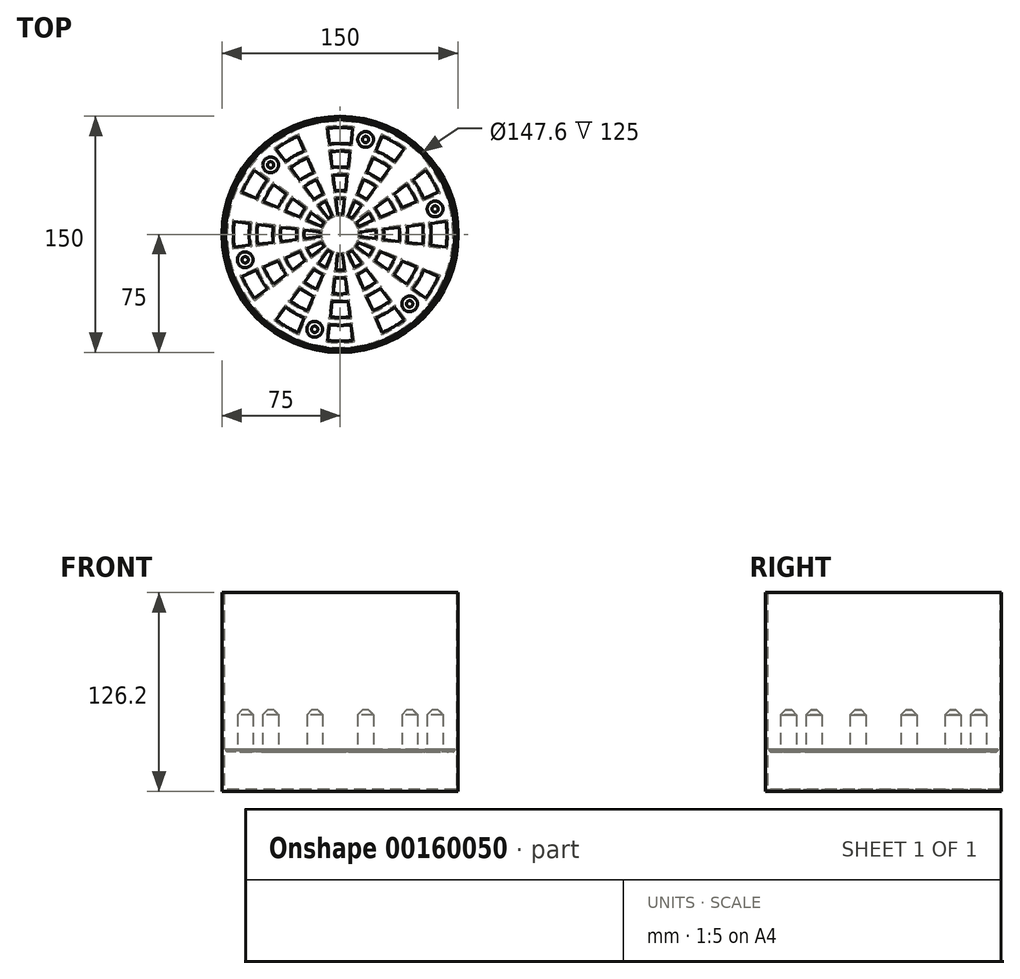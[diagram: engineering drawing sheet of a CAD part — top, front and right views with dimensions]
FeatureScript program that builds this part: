
annotation { "Feature Type Name" : "Feature", "Feature Type Description" : "" }
export const myFeature = defineFeature(function(context is Context, id is Id, definition is map)
    precondition{}
    {
        {
            var Q0;
            Q0=qCreatedBy(makeId("Top.planeOp"),FACE);
            var sketch = newSketch(context, id + "F0", { "sketchPlane" : qUnion([Q0])});
            skCircle(sketch, "E0", {"center": v(0, 0) * mm, "radius": 75 * mm});
            skSolve(sketch);
        }
        {
            var Q0;
            Q0 = qSketchRegion(id + "F0", true);
            extrude(context, id + "F1", {"entities" : qUnion([Q0]), "depth" : 1.2 * mm, "offsetDistance" : 25 * mm});
        }
        {
            var Q0;
            Q0=makeQuery(id+"F1.opExtrude","CAP_FACE",FACE,{"disambiguationData":[OSD([sQuery(id+"F0.wireOp",EDGE,"E0")])],"isStart":false});
            var sketch = newSketch(context, id + "F2", { "sketchPlane" : qUnion([Q0])});
            skCircle(sketch, "E1", {"center": v(0, 0) * mm, "radius": 75 * mm});
            skCircle(sketch, "E2", {"center": v(0, 0) * mm, "radius": 73.8 * mm});
            skSolve(sketch);
        }
        {
            var Q0;
            Q0 = qSketchRegion(id + "F2", true);
            extrude(context, id + "F3", {"entities" : qUnion([Q0]), "operationType" : NewBodyOperationType.ADD, "depth" : 125 * mm, "offsetDistance" : 25 * mm});
        }
        {
            var Q0;
            Q0=qCreatedBy(makeId("Top.planeOp"),FACE);
            cPlane(context, id + "F4", {"entities" : qUnion([Q0]), "cplaneType" : CPlaneType.OFFSET, "offset" : 25 * mm, "width" : 150 * mm, "height" : 150 * mm});
        }
        {
            var Q0;
            Q0=qCreatedBy(id+"F4.planeOp",FACE);
            var sketch = newSketch(context, id + "F5", { "sketchPlane" : qUnion([Q0])});
            skCircle(sketch, "E3", {"center": v(0, 0) * mm, "radius": 72.8 * mm});
            skLineSegment(sketch, "E4", {"start": v(1.51, 12.71) * mm, "end": v(2.7, 22.64) * mm});
            skArc(sketch, "E5", {"start": v(8, 67.33) * mm, "mid": v(0, 67.8) * mm, "end": v(-8, 67.33) * mm});
            skLineSegment(sketch, "E6.MirrorCS", {"start": v(-1.51, 12.71) * mm, "end": v(-2.7, 22.64) * mm});
            skArc(sketch, "E7", {"start": v(6.82, 57.4) * mm, "mid": v(0, 57.8) * mm, "end": v(-6.82, 57.4) * mm});
            skArc(sketch, "E8", {"start": v(6.23, 52.43) * mm, "mid": v(0, 52.8) * mm, "end": v(-6.23, 52.43) * mm});
            skArc(sketch, "E9", {"start": v(5.05, 42.5) * mm, "mid": v(0, 42.8) * mm, "end": v(-5.05, 42.5) * mm});
            skArc(sketch, "E10", {"start": v(4.46, 37.54) * mm, "mid": v(0, 37.8) * mm, "end": v(-4.46, 37.54) * mm});
            skArc(sketch, "E11", {"start": v(3.28, 27.6) * mm, "mid": v(0, 27.8) * mm, "end": v(-3.28, 27.6) * mm});
            skArc(sketch, "E12", {"start": v(2.7, 22.64) * mm, "mid": v(0, 22.8) * mm, "end": v(-2.7, 22.64) * mm});
            skArc(sketch, "E13", {"start": v(1.51, 12.71) * mm, "mid": v(0, 12.8) * mm, "end": v(-1.51, 12.71) * mm});
            skLineSegment(sketch, "E14.trimOffspring", {"start": v(-3.28, 27.6) * mm, "end": v(-4.46, 37.54) * mm});
            skLineSegment(sketch, "E15.trimOffspring", {"start": v(3.28, 27.6) * mm, "end": v(4.46, 37.54) * mm});
            skLineSegment(sketch, "E16.trimOffspring", {"start": v(-5.05, 42.5) * mm, "end": v(-6.23, 52.43) * mm});
            skLineSegment(sketch, "E17.trimOffspring", {"start": v(5.05, 42.5) * mm, "end": v(6.23, 52.43) * mm});
            skLineSegment(sketch, "E18.trimOffspring", {"start": v(-6.82, 57.4) * mm, "end": v(-8, 67.33) * mm});
            skLineSegment(sketch, "E19.trimOffspring", {"start": v(6.82, 57.4) * mm, "end": v(8, 67.33) * mm});
            skArc(sketch, "E20.1.0", {"start": v(-22.8, 53.12) * mm, "mid": v(-28.9, 50.06) * mm, "end": v(-34.6, 46.3) * mm});
            skArc(sketch, "E20.1.1", {"start": v(-16.88, 39.33) * mm, "mid": v(-21.4, 37.07) * mm, "end": v(-25.62, 34.28) * mm});
            skArc(sketch, "E20.1.2", {"start": v(-14.9, 34.74) * mm, "mid": v(-18.9, 32.74) * mm, "end": v(-22.63, 30.28) * mm});
            skArc(sketch, "E20.1.3", {"start": v(-9, 20.95) * mm, "mid": v(-11.4, 19.75) * mm, "end": v(-13.65, 18.26) * mm});
            skLineSegment(sketch, "E20.1.4", {"start": v(-22.8, 53.12) * mm, "end": v(-26.73, 62.3) * mm});
            skLineSegment(sketch, "E20.1.5", {"start": v(-10.96, 25.55) * mm, "end": v(-14.9, 34.74) * mm});
            skArc(sketch, "E20.1.6", {"start": v(-26.73, 62.3) * mm, "mid": v(-33.9, 58.72) * mm, "end": v(-40.6, 54.3) * mm});
            skLineSegment(sketch, "E20.1.7", {"start": v(-16.64, 22.27) * mm, "end": v(-22.63, 30.28) * mm});
            skLineSegment(sketch, "E20.1.8", {"start": v(-25.62, 34.28) * mm, "end": v(-31.61, 42.3) * mm});
            skArc(sketch, "E20.1.9", {"start": v(-20.82, 48.52) * mm, "mid": v(-26.4, 45.73) * mm, "end": v(-31.61, 42.3) * mm});
            skLineSegment(sketch, "E20.1.10", {"start": v(-7.66, 10.25) * mm, "end": v(-13.65, 18.26) * mm});
            skLineSegment(sketch, "E20.1.11", {"start": v(-34.6, 46.3) * mm, "end": v(-40.6, 54.3) * mm});
            skArc(sketch, "E20.1.12", {"start": v(-10.96, 25.55) * mm, "mid": v(-13.9, 24.08) * mm, "end": v(-16.64, 22.27) * mm});
            skLineSegment(sketch, "E20.1.13", {"start": v(-16.88, 39.33) * mm, "end": v(-20.82, 48.52) * mm});
            skLineSegment(sketch, "E20.1.14", {"start": v(-5.05, 11.76) * mm, "end": v(-9, 20.95) * mm});
            skArc(sketch, "E20.1.15", {"start": v(-5.05, 11.76) * mm, "mid": v(-6.4, 11.09) * mm, "end": v(-7.66, 10.25) * mm});
            skArc(sketch, "E20.2.0", {"start": v(-46.3, 34.6) * mm, "mid": v(-50.06, 28.9) * mm, "end": v(-53.12, 22.8) * mm});
            skArc(sketch, "E20.2.1", {"start": v(-34.28, 25.62) * mm, "mid": v(-37.07, 21.4) * mm, "end": v(-39.33, 16.88) * mm});
            skArc(sketch, "E20.2.2", {"start": v(-30.28, 22.63) * mm, "mid": v(-32.74, 18.9) * mm, "end": v(-34.74, 14.9) * mm});
            skArc(sketch, "E20.2.3", {"start": v(-18.26, 13.65) * mm, "mid": v(-19.75, 11.4) * mm, "end": v(-20.95, 9) * mm});
            skLineSegment(sketch, "E20.2.4", {"start": v(-46.3, 34.6) * mm, "end": v(-54.3, 40.6) * mm});
            skLineSegment(sketch, "E20.2.5", {"start": v(-22.27, 16.64) * mm, "end": v(-30.28, 22.63) * mm});
            skArc(sketch, "E20.2.6", {"start": v(-54.3, 40.6) * mm, "mid": v(-58.72, 33.9) * mm, "end": v(-62.3, 26.73) * mm});
            skLineSegment(sketch, "E20.2.7", {"start": v(-25.55, 10.96) * mm, "end": v(-34.74, 14.9) * mm});
            skLineSegment(sketch, "E20.2.8", {"start": v(-39.33, 16.88) * mm, "end": v(-48.52, 20.82) * mm});
            skArc(sketch, "E20.2.9", {"start": v(-42.3, 31.61) * mm, "mid": v(-45.73, 26.4) * mm, "end": v(-48.52, 20.82) * mm});
            skLineSegment(sketch, "E20.2.10", {"start": v(-11.76, 5.05) * mm, "end": v(-20.95, 9) * mm});
            skLineSegment(sketch, "E20.2.11", {"start": v(-53.12, 22.8) * mm, "end": v(-62.3, 26.73) * mm});
            skArc(sketch, "E20.2.12", {"start": v(-22.27, 16.64) * mm, "mid": v(-24.08, 13.9) * mm, "end": v(-25.55, 10.96) * mm});
            skLineSegment(sketch, "E20.2.13", {"start": v(-34.28, 25.62) * mm, "end": v(-42.3, 31.61) * mm});
            skLineSegment(sketch, "E20.2.14", {"start": v(-10.25, 7.66) * mm, "end": v(-18.26, 13.65) * mm});
            skArc(sketch, "E20.2.15", {"start": v(-10.25, 7.66) * mm, "mid": v(-11.09, 6.4) * mm, "end": v(-11.76, 5.05) * mm});
            skArc(sketch, "E20.3.0", {"start": v(-57.4, 6.82) * mm, "mid": v(-57.8, 0) * mm, "end": v(-57.4, -6.82) * mm});
            skArc(sketch, "E20.3.1", {"start": v(-42.5, 5.05) * mm, "mid": v(-42.8, 0) * mm, "end": v(-42.5, -5.05) * mm});
            skArc(sketch, "E20.3.2", {"start": v(-37.54, 4.46) * mm, "mid": v(-37.8, 0) * mm, "end": v(-37.54, -4.46) * mm});
            skArc(sketch, "E20.3.3", {"start": v(-22.64, 2.7) * mm, "mid": v(-22.8, 0) * mm, "end": v(-22.64, -2.7) * mm});
            skLineSegment(sketch, "E20.3.4", {"start": v(-57.4, 6.82) * mm, "end": v(-67.33, 8) * mm});
            skLineSegment(sketch, "E20.3.5", {"start": v(-27.6, 3.28) * mm, "end": v(-37.54, 4.46) * mm});
            skArc(sketch, "E20.3.6", {"start": v(-67.33, 8) * mm, "mid": v(-67.8, 0) * mm, "end": v(-67.33, -8) * mm});
            skLineSegment(sketch, "E20.3.7", {"start": v(-27.6, -3.28) * mm, "end": v(-37.54, -4.46) * mm});
            skLineSegment(sketch, "E20.3.8", {"start": v(-42.5, -5.05) * mm, "end": v(-52.43, -6.23) * mm});
            skArc(sketch, "E20.3.9", {"start": v(-52.43, 6.23) * mm, "mid": v(-52.8, 0) * mm, "end": v(-52.43, -6.23) * mm});
            skLineSegment(sketch, "E20.3.10", {"start": v(-12.71, -1.51) * mm, "end": v(-22.64, -2.7) * mm});
            skLineSegment(sketch, "E20.3.11", {"start": v(-57.4, -6.82) * mm, "end": v(-67.33, -8) * mm});
            skArc(sketch, "E20.3.12", {"start": v(-27.6, 3.28) * mm, "mid": v(-27.8, 0) * mm, "end": v(-27.6, -3.28) * mm});
            skLineSegment(sketch, "E20.3.13", {"start": v(-42.5, 5.05) * mm, "end": v(-52.43, 6.23) * mm});
            skLineSegment(sketch, "E20.3.14", {"start": v(-12.71, 1.51) * mm, "end": v(-22.64, 2.7) * mm});
            skArc(sketch, "E20.3.15", {"start": v(-12.71, 1.51) * mm, "mid": v(-12.8, 0) * mm, "end": v(-12.71, -1.51) * mm});
            skArc(sketch, "E20.4.0", {"start": v(-53.12, -22.8) * mm, "mid": v(-50.06, -28.9) * mm, "end": v(-46.3, -34.6) * mm});
            skArc(sketch, "E20.4.1", {"start": v(-39.33, -16.88) * mm, "mid": v(-37.07, -21.4) * mm, "end": v(-34.28, -25.62) * mm});
            skArc(sketch, "E20.4.2", {"start": v(-34.74, -14.9) * mm, "mid": v(-32.74, -18.9) * mm, "end": v(-30.28, -22.63) * mm});
            skArc(sketch, "E20.4.3", {"start": v(-20.95, -9) * mm, "mid": v(-19.75, -11.4) * mm, "end": v(-18.26, -13.65) * mm});
            skLineSegment(sketch, "E20.4.4", {"start": v(-53.12, -22.8) * mm, "end": v(-62.3, -26.73) * mm});
            skLineSegment(sketch, "E20.4.5", {"start": v(-25.55, -10.96) * mm, "end": v(-34.74, -14.9) * mm});
            skArc(sketch, "E20.4.6", {"start": v(-62.3, -26.73) * mm, "mid": v(-58.72, -33.9) * mm, "end": v(-54.3, -40.6) * mm});
            skLineSegment(sketch, "E20.4.7", {"start": v(-22.27, -16.64) * mm, "end": v(-30.28, -22.63) * mm});
            skLineSegment(sketch, "E20.4.8", {"start": v(-34.28, -25.62) * mm, "end": v(-42.3, -31.61) * mm});
            skArc(sketch, "E20.4.9", {"start": v(-48.52, -20.82) * mm, "mid": v(-45.73, -26.4) * mm, "end": v(-42.3, -31.61) * mm});
            skLineSegment(sketch, "E20.4.10", {"start": v(-10.25, -7.66) * mm, "end": v(-18.26, -13.65) * mm});
            skLineSegment(sketch, "E20.4.11", {"start": v(-46.3, -34.6) * mm, "end": v(-54.3, -40.6) * mm});
            skArc(sketch, "E20.4.12", {"start": v(-25.55, -10.96) * mm, "mid": v(-24.08, -13.9) * mm, "end": v(-22.27, -16.64) * mm});
            skLineSegment(sketch, "E20.4.13", {"start": v(-39.33, -16.88) * mm, "end": v(-48.52, -20.82) * mm});
            skLineSegment(sketch, "E20.4.14", {"start": v(-11.76, -5.05) * mm, "end": v(-20.95, -9) * mm});
            skArc(sketch, "E20.4.15", {"start": v(-11.76, -5.05) * mm, "mid": v(-11.09, -6.4) * mm, "end": v(-10.25, -7.66) * mm});
            skArc(sketch, "E20.5.0", {"start": v(-34.6, -46.3) * mm, "mid": v(-28.9, -50.06) * mm, "end": v(-22.8, -53.12) * mm});
            skArc(sketch, "E20.5.1", {"start": v(-25.62, -34.28) * mm, "mid": v(-21.4, -37.07) * mm, "end": v(-16.88, -39.33) * mm});
            skArc(sketch, "E20.5.2", {"start": v(-22.63, -30.28) * mm, "mid": v(-18.9, -32.74) * mm, "end": v(-14.9, -34.74) * mm});
            skArc(sketch, "E20.5.3", {"start": v(-13.65, -18.26) * mm, "mid": v(-11.4, -19.75) * mm, "end": v(-9, -20.95) * mm});
            skLineSegment(sketch, "E20.5.4", {"start": v(-34.6, -46.3) * mm, "end": v(-40.6, -54.3) * mm});
            skLineSegment(sketch, "E20.5.5", {"start": v(-16.64, -22.27) * mm, "end": v(-22.63, -30.28) * mm});
            skArc(sketch, "E20.5.6", {"start": v(-40.6, -54.3) * mm, "mid": v(-33.9, -58.72) * mm, "end": v(-26.73, -62.3) * mm});
            skLineSegment(sketch, "E20.5.7", {"start": v(-10.96, -25.55) * mm, "end": v(-14.9, -34.74) * mm});
            skLineSegment(sketch, "E20.5.8", {"start": v(-16.88, -39.33) * mm, "end": v(-20.82, -48.52) * mm});
            skArc(sketch, "E20.5.9", {"start": v(-31.61, -42.3) * mm, "mid": v(-26.4, -45.73) * mm, "end": v(-20.82, -48.52) * mm});
            skLineSegment(sketch, "E20.5.10", {"start": v(-5.05, -11.76) * mm, "end": v(-9, -20.95) * mm});
            skLineSegment(sketch, "E20.5.11", {"start": v(-22.8, -53.12) * mm, "end": v(-26.73, -62.3) * mm});
            skArc(sketch, "E20.5.12", {"start": v(-16.64, -22.27) * mm, "mid": v(-13.9, -24.08) * mm, "end": v(-10.96, -25.55) * mm});
            skLineSegment(sketch, "E20.5.13", {"start": v(-25.62, -34.28) * mm, "end": v(-31.61, -42.3) * mm});
            skLineSegment(sketch, "E20.5.14", {"start": v(-7.66, -10.25) * mm, "end": v(-13.65, -18.26) * mm});
            skArc(sketch, "E20.5.15", {"start": v(-7.66, -10.25) * mm, "mid": v(-6.4, -11.09) * mm, "end": v(-5.05, -11.76) * mm});
            skArc(sketch, "E20.6.0", {"start": v(-6.82, -57.4) * mm, "mid": v(0, -57.8) * mm, "end": v(6.82, -57.4) * mm});
            skArc(sketch, "E20.6.1", {"start": v(-5.05, -42.5) * mm, "mid": v(0, -42.8) * mm, "end": v(5.05, -42.5) * mm});
            skArc(sketch, "E20.6.2", {"start": v(-4.46, -37.54) * mm, "mid": v(0, -37.8) * mm, "end": v(4.46, -37.54) * mm});
            skArc(sketch, "E20.6.3", {"start": v(-2.7, -22.64) * mm, "mid": v(0, -22.8) * mm, "end": v(2.7, -22.64) * mm});
            skLineSegment(sketch, "E20.6.4", {"start": v(-6.82, -57.4) * mm, "end": v(-8, -67.33) * mm});
            skLineSegment(sketch, "E20.6.5", {"start": v(-3.28, -27.6) * mm, "end": v(-4.46, -37.54) * mm});
            skArc(sketch, "E20.6.6", {"start": v(-8, -67.33) * mm, "mid": v(0, -67.8) * mm, "end": v(8, -67.33) * mm});
            skLineSegment(sketch, "E20.6.7", {"start": v(3.28, -27.6) * mm, "end": v(4.46, -37.54) * mm});
            skLineSegment(sketch, "E20.6.8", {"start": v(5.05, -42.5) * mm, "end": v(6.23, -52.43) * mm});
            skArc(sketch, "E20.6.9", {"start": v(-6.23, -52.43) * mm, "mid": v(0, -52.8) * mm, "end": v(6.23, -52.43) * mm});
            skLineSegment(sketch, "E20.6.10", {"start": v(1.51, -12.71) * mm, "end": v(2.7, -22.64) * mm});
            skLineSegment(sketch, "E20.6.11", {"start": v(6.82, -57.4) * mm, "end": v(8, -67.33) * mm});
            skArc(sketch, "E20.6.12", {"start": v(-3.28, -27.6) * mm, "mid": v(0, -27.8) * mm, "end": v(3.28, -27.6) * mm});
            skLineSegment(sketch, "E20.6.13", {"start": v(-5.05, -42.5) * mm, "end": v(-6.23, -52.43) * mm});
            skLineSegment(sketch, "E20.6.14", {"start": v(-1.51, -12.71) * mm, "end": v(-2.7, -22.64) * mm});
            skArc(sketch, "E20.6.15", {"start": v(-1.51, -12.71) * mm, "mid": v(0, -12.8) * mm, "end": v(1.51, -12.71) * mm});
            skArc(sketch, "E20.7.0", {"start": v(22.8, -53.12) * mm, "mid": v(28.9, -50.06) * mm, "end": v(34.6, -46.3) * mm});
            skArc(sketch, "E20.7.1", {"start": v(16.88, -39.33) * mm, "mid": v(21.4, -37.07) * mm, "end": v(25.62, -34.28) * mm});
            skArc(sketch, "E20.7.2", {"start": v(14.9, -34.74) * mm, "mid": v(18.9, -32.74) * mm, "end": v(22.63, -30.28) * mm});
            skArc(sketch, "E20.7.3", {"start": v(9, -20.95) * mm, "mid": v(11.4, -19.75) * mm, "end": v(13.65, -18.26) * mm});
            skLineSegment(sketch, "E20.7.4", {"start": v(22.8, -53.12) * mm, "end": v(26.73, -62.3) * mm});
            skLineSegment(sketch, "E20.7.5", {"start": v(10.96, -25.55) * mm, "end": v(14.9, -34.74) * mm});
            skArc(sketch, "E20.7.6", {"start": v(26.73, -62.3) * mm, "mid": v(33.9, -58.72) * mm, "end": v(40.6, -54.3) * mm});
            skLineSegment(sketch, "E20.7.7", {"start": v(16.64, -22.27) * mm, "end": v(22.63, -30.28) * mm});
            skLineSegment(sketch, "E20.7.8", {"start": v(25.62, -34.28) * mm, "end": v(31.61, -42.3) * mm});
            skArc(sketch, "E20.7.9", {"start": v(20.82, -48.52) * mm, "mid": v(26.4, -45.73) * mm, "end": v(31.61, -42.3) * mm});
            skLineSegment(sketch, "E20.7.10", {"start": v(7.66, -10.25) * mm, "end": v(13.65, -18.26) * mm});
            skLineSegment(sketch, "E20.7.11", {"start": v(34.6, -46.3) * mm, "end": v(40.6, -54.3) * mm});
            skArc(sketch, "E20.7.12", {"start": v(10.96, -25.55) * mm, "mid": v(13.9, -24.08) * mm, "end": v(16.64, -22.27) * mm});
            skLineSegment(sketch, "E20.7.13", {"start": v(16.88, -39.33) * mm, "end": v(20.82, -48.52) * mm});
            skLineSegment(sketch, "E20.7.14", {"start": v(5.05, -11.76) * mm, "end": v(9, -20.95) * mm});
            skArc(sketch, "E20.7.15", {"start": v(5.05, -11.76) * mm, "mid": v(6.4, -11.09) * mm, "end": v(7.66, -10.25) * mm});
            skArc(sketch, "E20.8.0", {"start": v(46.3, -34.6) * mm, "mid": v(50.06, -28.9) * mm, "end": v(53.12, -22.8) * mm});
            skArc(sketch, "E20.8.1", {"start": v(34.28, -25.62) * mm, "mid": v(37.07, -21.4) * mm, "end": v(39.33, -16.88) * mm});
            skArc(sketch, "E20.8.2", {"start": v(30.28, -22.63) * mm, "mid": v(32.74, -18.9) * mm, "end": v(34.74, -14.9) * mm});
            skArc(sketch, "E20.8.3", {"start": v(18.26, -13.65) * mm, "mid": v(19.75, -11.4) * mm, "end": v(20.95, -9) * mm});
            skLineSegment(sketch, "E20.8.4", {"start": v(46.3, -34.6) * mm, "end": v(54.3, -40.6) * mm});
            skLineSegment(sketch, "E20.8.5", {"start": v(22.27, -16.64) * mm, "end": v(30.28, -22.63) * mm});
            skArc(sketch, "E20.8.6", {"start": v(54.3, -40.6) * mm, "mid": v(58.72, -33.9) * mm, "end": v(62.3, -26.73) * mm});
            skLineSegment(sketch, "E20.8.7", {"start": v(25.55, -10.96) * mm, "end": v(34.74, -14.9) * mm});
            skLineSegment(sketch, "E20.8.8", {"start": v(39.33, -16.88) * mm, "end": v(48.52, -20.82) * mm});
            skArc(sketch, "E20.8.9", {"start": v(42.3, -31.61) * mm, "mid": v(45.73, -26.4) * mm, "end": v(48.52, -20.82) * mm});
            skLineSegment(sketch, "E20.8.10", {"start": v(11.76, -5.05) * mm, "end": v(20.95, -9) * mm});
            skLineSegment(sketch, "E20.8.11", {"start": v(53.12, -22.8) * mm, "end": v(62.3, -26.73) * mm});
            skArc(sketch, "E20.8.12", {"start": v(22.27, -16.64) * mm, "mid": v(24.08, -13.9) * mm, "end": v(25.55, -10.96) * mm});
            skLineSegment(sketch, "E20.8.13", {"start": v(34.28, -25.62) * mm, "end": v(42.3, -31.61) * mm});
            skLineSegment(sketch, "E20.8.14", {"start": v(10.25, -7.66) * mm, "end": v(18.26, -13.65) * mm});
            skArc(sketch, "E20.8.15", {"start": v(10.25, -7.66) * mm, "mid": v(11.09, -6.4) * mm, "end": v(11.76, -5.05) * mm});
            skArc(sketch, "E20.9.0", {"start": v(57.4, -6.82) * mm, "mid": v(57.8, 0) * mm, "end": v(57.4, 6.82) * mm});
            skArc(sketch, "E20.9.1", {"start": v(42.5, -5.05) * mm, "mid": v(42.8, 0) * mm, "end": v(42.5, 5.05) * mm});
            skArc(sketch, "E20.9.2", {"start": v(37.54, -4.46) * mm, "mid": v(37.8, 0) * mm, "end": v(37.54, 4.46) * mm});
            skArc(sketch, "E20.9.3", {"start": v(22.64, -2.7) * mm, "mid": v(22.8, 0) * mm, "end": v(22.64, 2.7) * mm});
            skLineSegment(sketch, "E20.9.4", {"start": v(57.4, -6.82) * mm, "end": v(67.33, -8) * mm});
            skLineSegment(sketch, "E20.9.5", {"start": v(27.6, -3.28) * mm, "end": v(37.54, -4.46) * mm});
            skArc(sketch, "E20.9.6", {"start": v(67.33, -8) * mm, "mid": v(67.8, 0) * mm, "end": v(67.33, 8) * mm});
            skLineSegment(sketch, "E20.9.7", {"start": v(27.6, 3.28) * mm, "end": v(37.54, 4.46) * mm});
            skLineSegment(sketch, "E20.9.8", {"start": v(42.5, 5.05) * mm, "end": v(52.43, 6.23) * mm});
            skArc(sketch, "E20.9.9", {"start": v(52.43, -6.23) * mm, "mid": v(52.8, 0) * mm, "end": v(52.43, 6.23) * mm});
            skLineSegment(sketch, "E20.9.10", {"start": v(12.71, 1.51) * mm, "end": v(22.64, 2.7) * mm});
            skLineSegment(sketch, "E20.9.11", {"start": v(57.4, 6.82) * mm, "end": v(67.33, 8) * mm});
            skArc(sketch, "E20.9.12", {"start": v(27.6, -3.28) * mm, "mid": v(27.8, 0) * mm, "end": v(27.6, 3.28) * mm});
            skLineSegment(sketch, "E20.9.13", {"start": v(42.5, -5.05) * mm, "end": v(52.43, -6.23) * mm});
            skLineSegment(sketch, "E20.9.14", {"start": v(12.71, -1.51) * mm, "end": v(22.64, -2.7) * mm});
            skArc(sketch, "E20.9.15", {"start": v(12.71, -1.51) * mm, "mid": v(12.8, 0) * mm, "end": v(12.71, 1.51) * mm});
            skArc(sketch, "E21.4.10.0", {"start": v(39.33, 16.88) * mm, "mid": v(37.07, 21.4) * mm, "end": v(34.28, 25.62) * mm});
            skArc(sketch, "E21.8.10.0", {"start": v(34.74, 14.9) * mm, "mid": v(32.74, 18.9) * mm, "end": v(30.28, 22.63) * mm});
            skArc(sketch, "E21.12.10.0", {"start": v(20.95, 9) * mm, "mid": v(19.75, 11.4) * mm, "end": v(18.26, 13.65) * mm});
            skLineSegment(sketch, "E21.16.10.0", {"start": v(53.12, 22.8) * mm, "end": v(62.3, 26.73) * mm});
            skLineSegment(sketch, "E21.19.10.0", {"start": v(25.55, 10.96) * mm, "end": v(34.74, 14.9) * mm});
            skArc(sketch, "E21.22.10.0", {"start": v(62.3, 26.73) * mm, "mid": v(58.72, 33.9) * mm, "end": v(54.3, 40.6) * mm});
            skLineSegment(sketch, "E21.26.10.0", {"start": v(22.27, 16.64) * mm, "end": v(30.28, 22.63) * mm});
            skLineSegment(sketch, "E21.29.10.0", {"start": v(34.28, 25.62) * mm, "end": v(42.3, 31.61) * mm});
            skArc(sketch, "E21.32.10.0", {"start": v(48.52, 20.82) * mm, "mid": v(45.73, 26.4) * mm, "end": v(42.3, 31.61) * mm});
            skLineSegment(sketch, "E21.36.10.0", {"start": v(10.25, 7.66) * mm, "end": v(18.26, 13.65) * mm});
            skArc(sketch, "E21.37.10.0", {"start": v(53.12, 22.8) * mm, "mid": v(50.06, 28.9) * mm, "end": v(46.3, 34.6) * mm});
            skLineSegment(sketch, "E21.39.10.0", {"start": v(46.3, 34.6) * mm, "end": v(54.3, 40.6) * mm});
            skArc(sketch, "E21.42.10.0", {"start": v(25.55, 10.96) * mm, "mid": v(24.08, 13.9) * mm, "end": v(22.27, 16.64) * mm});
            skLineSegment(sketch, "E21.46.10.0", {"start": v(39.33, 16.88) * mm, "end": v(48.52, 20.82) * mm});
            skLineSegment(sketch, "E21.49.10.0", {"start": v(11.76, 5.05) * mm, "end": v(20.95, 9) * mm});
            skArc(sketch, "E21.52.10.0", {"start": v(11.76, 5.05) * mm, "mid": v(11.09, 6.4) * mm, "end": v(10.25, 7.66) * mm});
            skArc(sketch, "E21.4.11.0", {"start": v(25.62, 34.28) * mm, "mid": v(21.4, 37.07) * mm, "end": v(16.88, 39.33) * mm});
            skArc(sketch, "E21.8.11.0", {"start": v(22.63, 30.28) * mm, "mid": v(18.9, 32.74) * mm, "end": v(14.9, 34.74) * mm});
            skArc(sketch, "E21.12.11.0", {"start": v(13.65, 18.26) * mm, "mid": v(11.4, 19.75) * mm, "end": v(9, 20.95) * mm});
            skLineSegment(sketch, "E21.16.11.0", {"start": v(34.6, 46.3) * mm, "end": v(40.6, 54.3) * mm});
            skLineSegment(sketch, "E21.19.11.0", {"start": v(16.64, 22.27) * mm, "end": v(22.63, 30.28) * mm});
            skArc(sketch, "E21.22.11.0", {"start": v(40.6, 54.3) * mm, "mid": v(33.9, 58.72) * mm, "end": v(26.73, 62.3) * mm});
            skLineSegment(sketch, "E21.26.11.0", {"start": v(10.96, 25.55) * mm, "end": v(14.9, 34.74) * mm});
            skLineSegment(sketch, "E21.29.11.0", {"start": v(16.88, 39.33) * mm, "end": v(20.82, 48.52) * mm});
            skArc(sketch, "E21.32.11.0", {"start": v(31.61, 42.3) * mm, "mid": v(26.4, 45.73) * mm, "end": v(20.82, 48.52) * mm});
            skLineSegment(sketch, "E21.36.11.0", {"start": v(5.05, 11.76) * mm, "end": v(9, 20.95) * mm});
            skArc(sketch, "E21.37.11.0", {"start": v(34.6, 46.3) * mm, "mid": v(28.9, 50.06) * mm, "end": v(22.8, 53.12) * mm});
            skLineSegment(sketch, "E21.39.11.0", {"start": v(22.8, 53.12) * mm, "end": v(26.73, 62.3) * mm});
            skArc(sketch, "E21.42.11.0", {"start": v(16.64, 22.27) * mm, "mid": v(13.9, 24.08) * mm, "end": v(10.96, 25.55) * mm});
            skLineSegment(sketch, "E21.46.11.0", {"start": v(25.62, 34.28) * mm, "end": v(31.61, 42.3) * mm});
            skLineSegment(sketch, "E21.49.11.0", {"start": v(7.66, 10.25) * mm, "end": v(13.65, 18.26) * mm});
            skArc(sketch, "E21.52.11.0", {"start": v(7.66, 10.25) * mm, "mid": v(6.4, 11.09) * mm, "end": v(5.05, 11.76) * mm});
            skSolve(sketch);
        }
        {
            var Q0;
            Q0 = qSketchRegion(id + "F5", true);
            extrude(context, id + "F6", {"entities" : qUnion([Q0]), "depth" : 1.6 * mm, "offsetDistance" : 25 * mm});
        }
        {
            var Q0;
            Q0=makeQuery(id+"F6.opExtrude","CAP_FACE",FACE,{"disambiguationData":[OSD([sQuery(id+"F5.wireOp",EDGE,"E3"),sQuery(id+"F5.wireOp",EDGE,"E4"),sQuery(id+"F5.wireOp",EDGE,"E5"),sQuery(id+"F5.wireOp",EDGE,"E6.MirrorCS"),sQuery(id+"F5.wireOp",EDGE,"E7"),sQuery(id+"F5.wireOp",EDGE,"E8"),sQuery(id+"F5.wireOp",EDGE,"E9"),sQuery(id+"F5.wireOp",EDGE,"E10"),sQuery(id+"F5.wireOp",EDGE,"E11"),sQuery(id+"F5.wireOp",EDGE,"E12"),sQuery(id+"F5.wireOp",EDGE,"E13"),sQuery(id+"F5.wireOp",EDGE,"E14.trimOffspring"),sQuery(id+"F5.wireOp",EDGE,"E15.trimOffspring"),sQuery(id+"F5.wireOp",EDGE,"E16.trimOffspring"),sQuery(id+"F5.wireOp",EDGE,"E17.trimOffspring"),sQuery(id+"F5.wireOp",EDGE,"E18.trimOffspring"),sQuery(id+"F5.wireOp",EDGE,"E19.trimOffspring"),sQuery(id+"F5.wireOp",EDGE,"E20.1.0"),sQuery(id+"F5.wireOp",EDGE,"E20.1.1"),sQuery(id+"F5.wireOp",EDGE,"E20.1.2"),sQuery(id+"F5.wireOp",EDGE,"E20.1.3"),sQuery(id+"F5.wireOp",EDGE,"E20.1.4"),sQuery(id+"F5.wireOp",EDGE,"E20.1.5"),sQuery(id+"F5.wireOp",EDGE,"E20.1.6"),sQuery(id+"F5.wireOp",EDGE,"E20.1.7"),sQuery(id+"F5.wireOp",EDGE,"E20.1.8"),sQuery(id+"F5.wireOp",EDGE,"E20.1.9"),sQuery(id+"F5.wireOp",EDGE,"E20.1.10"),sQuery(id+"F5.wireOp",EDGE,"E20.1.11"),sQuery(id+"F5.wireOp",EDGE,"E20.1.12"),sQuery(id+"F5.wireOp",EDGE,"E20.1.13"),sQuery(id+"F5.wireOp",EDGE,"E20.1.14"),sQuery(id+"F5.wireOp",EDGE,"E20.1.15"),sQuery(id+"F5.wireOp",EDGE,"E20.2.0"),sQuery(id+"F5.wireOp",EDGE,"E20.2.1"),sQuery(id+"F5.wireOp",EDGE,"E20.2.2"),sQuery(id+"F5.wireOp",EDGE,"E20.2.3"),sQuery(id+"F5.wireOp",EDGE,"E20.2.4"),sQuery(id+"F5.wireOp",EDGE,"E20.2.5"),sQuery(id+"F5.wireOp",EDGE,"E20.2.6"),sQuery(id+"F5.wireOp",EDGE,"E20.2.7"),sQuery(id+"F5.wireOp",EDGE,"E20.2.8"),sQuery(id+"F5.wireOp",EDGE,"E20.2.9"),sQuery(id+"F5.wireOp",EDGE,"E20.2.10"),sQuery(id+"F5.wireOp",EDGE,"E20.2.11"),sQuery(id+"F5.wireOp",EDGE,"E20.2.12"),sQuery(id+"F5.wireOp",EDGE,"E20.2.13"),sQuery(id+"F5.wireOp",EDGE,"E20.2.14"),sQuery(id+"F5.wireOp",EDGE,"E20.2.15"),sQuery(id+"F5.wireOp",EDGE,"E20.3.0"),sQuery(id+"F5.wireOp",EDGE,"E20.3.1"),sQuery(id+"F5.wireOp",EDGE,"E20.3.2"),sQuery(id+"F5.wireOp",EDGE,"E20.3.3"),sQuery(id+"F5.wireOp",EDGE,"E20.3.4"),sQuery(id+"F5.wireOp",EDGE,"E20.3.5"),sQuery(id+"F5.wireOp",EDGE,"E20.3.6"),sQuery(id+"F5.wireOp",EDGE,"E20.3.7"),sQuery(id+"F5.wireOp",EDGE,"E20.3.8"),sQuery(id+"F5.wireOp",EDGE,"E20.3.9"),sQuery(id+"F5.wireOp",EDGE,"E20.3.10"),sQuery(id+"F5.wireOp",EDGE,"E20.3.11"),sQuery(id+"F5.wireOp",EDGE,"E20.3.12"),sQuery(id+"F5.wireOp",EDGE,"E20.3.13"),sQuery(id+"F5.wireOp",EDGE,"E20.3.14"),sQuery(id+"F5.wireOp",EDGE,"E20.3.15"),sQuery(id+"F5.wireOp",EDGE,"E20.4.0"),sQuery(id+"F5.wireOp",EDGE,"E20.4.1"),sQuery(id+"F5.wireOp",EDGE,"E20.4.2"),sQuery(id+"F5.wireOp",EDGE,"E20.4.3"),sQuery(id+"F5.wireOp",EDGE,"E20.4.4"),sQuery(id+"F5.wireOp",EDGE,"E20.4.5"),sQuery(id+"F5.wireOp",EDGE,"E20.4.6"),sQuery(id+"F5.wireOp",EDGE,"E20.4.7"),sQuery(id+"F5.wireOp",EDGE,"E20.4.8"),sQuery(id+"F5.wireOp",EDGE,"E20.4.9"),sQuery(id+"F5.wireOp",EDGE,"E20.4.10"),sQuery(id+"F5.wireOp",EDGE,"E20.4.11"),sQuery(id+"F5.wireOp",EDGE,"E20.4.12"),sQuery(id+"F5.wireOp",EDGE,"E20.4.13"),sQuery(id+"F5.wireOp",EDGE,"E20.4.14"),sQuery(id+"F5.wireOp",EDGE,"E20.4.15"),sQuery(id+"F5.wireOp",EDGE,"E20.5.0"),sQuery(id+"F5.wireOp",EDGE,"E20.5.1"),sQuery(id+"F5.wireOp",EDGE,"E20.5.2"),sQuery(id+"F5.wireOp",EDGE,"E20.5.3"),sQuery(id+"F5.wireOp",EDGE,"E20.5.4"),sQuery(id+"F5.wireOp",EDGE,"E20.5.5"),sQuery(id+"F5.wireOp",EDGE,"E20.5.6"),sQuery(id+"F5.wireOp",EDGE,"E20.5.7"),sQuery(id+"F5.wireOp",EDGE,"E20.5.8"),sQuery(id+"F5.wireOp",EDGE,"E20.5.9"),sQuery(id+"F5.wireOp",EDGE,"E20.5.10"),sQuery(id+"F5.wireOp",EDGE,"E20.5.11"),sQuery(id+"F5.wireOp",EDGE,"E20.5.12"),sQuery(id+"F5.wireOp",EDGE,"E20.5.13"),sQuery(id+"F5.wireOp",EDGE,"E20.5.14"),sQuery(id+"F5.wireOp",EDGE,"E20.5.15"),sQuery(id+"F5.wireOp",EDGE,"E20.6.0"),sQuery(id+"F5.wireOp",EDGE,"E20.6.1"),sQuery(id+"F5.wireOp",EDGE,"E20.6.2"),sQuery(id+"F5.wireOp",EDGE,"E20.6.3"),sQuery(id+"F5.wireOp",EDGE,"E20.6.4"),sQuery(id+"F5.wireOp",EDGE,"E20.6.5"),sQuery(id+"F5.wireOp",EDGE,"E20.6.6"),sQuery(id+"F5.wireOp",EDGE,"E20.6.7"),sQuery(id+"F5.wireOp",EDGE,"E20.6.8"),sQuery(id+"F5.wireOp",EDGE,"E20.6.9"),sQuery(id+"F5.wireOp",EDGE,"E20.6.10"),sQuery(id+"F5.wireOp",EDGE,"E20.6.11"),sQuery(id+"F5.wireOp",EDGE,"E20.6.12"),sQuery(id+"F5.wireOp",EDGE,"E20.6.13"),sQuery(id+"F5.wireOp",EDGE,"E20.6.14"),sQuery(id+"F5.wireOp",EDGE,"E20.6.15"),sQuery(id+"F5.wireOp",EDGE,"E20.7.0"),sQuery(id+"F5.wireOp",EDGE,"E20.7.1"),sQuery(id+"F5.wireOp",EDGE,"E20.7.2"),sQuery(id+"F5.wireOp",EDGE,"E20.7.3"),sQuery(id+"F5.wireOp",EDGE,"E20.7.4"),sQuery(id+"F5.wireOp",EDGE,"E20.7.5"),sQuery(id+"F5.wireOp",EDGE,"E20.7.6"),sQuery(id+"F5.wireOp",EDGE,"E20.7.7"),sQuery(id+"F5.wireOp",EDGE,"E20.7.8"),sQuery(id+"F5.wireOp",EDGE,"E20.7.9"),sQuery(id+"F5.wireOp",EDGE,"E20.7.10"),sQuery(id+"F5.wireOp",EDGE,"E20.7.11"),sQuery(id+"F5.wireOp",EDGE,"E20.7.12"),sQuery(id+"F5.wireOp",EDGE,"E20.7.13"),sQuery(id+"F5.wireOp",EDGE,"E20.7.14"),sQuery(id+"F5.wireOp",EDGE,"E20.7.15"),sQuery(id+"F5.wireOp",EDGE,"E20.8.0"),sQuery(id+"F5.wireOp",EDGE,"E20.8.1"),sQuery(id+"F5.wireOp",EDGE,"E20.8.2"),sQuery(id+"F5.wireOp",EDGE,"E20.8.3"),sQuery(id+"F5.wireOp",EDGE,"E20.8.4"),sQuery(id+"F5.wireOp",EDGE,"E20.8.5"),sQuery(id+"F5.wireOp",EDGE,"E20.8.6"),sQuery(id+"F5.wireOp",EDGE,"E20.8.7"),sQuery(id+"F5.wireOp",EDGE,"E20.8.8"),sQuery(id+"F5.wireOp",EDGE,"E20.8.9"),sQuery(id+"F5.wireOp",EDGE,"E20.8.10"),sQuery(id+"F5.wireOp",EDGE,"E20.8.11"),sQuery(id+"F5.wireOp",EDGE,"E20.8.12"),sQuery(id+"F5.wireOp",EDGE,"E20.8.13"),sQuery(id+"F5.wireOp",EDGE,"E20.8.14"),sQuery(id+"F5.wireOp",EDGE,"E20.8.15"),sQuery(id+"F5.wireOp",EDGE,"E20.9.0"),sQuery(id+"F5.wireOp",EDGE,"E20.9.1"),sQuery(id+"F5.wireOp",EDGE,"E20.9.2"),sQuery(id+"F5.wireOp",EDGE,"E20.9.3"),sQuery(id+"F5.wireOp",EDGE,"E20.9.4"),sQuery(id+"F5.wireOp",EDGE,"E20.9.5"),sQuery(id+"F5.wireOp",EDGE,"E20.9.6"),sQuery(id+"F5.wireOp",EDGE,"E20.9.7"),sQuery(id+"F5.wireOp",EDGE,"E20.9.8"),sQuery(id+"F5.wireOp",EDGE,"E20.9.9"),sQuery(id+"F5.wireOp",EDGE,"E20.9.10"),sQuery(id+"F5.wireOp",EDGE,"E20.9.11"),sQuery(id+"F5.wireOp",EDGE,"E20.9.12"),sQuery(id+"F5.wireOp",EDGE,"E20.9.13"),sQuery(id+"F5.wireOp",EDGE,"E20.9.14"),sQuery(id+"F5.wireOp",EDGE,"E20.9.15"),sQuery(id+"F5.wireOp",EDGE,"E21.4.10.0"),sQuery(id+"F5.wireOp",EDGE,"E21.8.10.0"),sQuery(id+"F5.wireOp",EDGE,"E21.12.10.0"),sQuery(id+"F5.wireOp",EDGE,"E21.16.10.0"),sQuery(id+"F5.wireOp",EDGE,"E21.19.10.0"),sQuery(id+"F5.wireOp",EDGE,"E21.22.10.0"),sQuery(id+"F5.wireOp",EDGE,"E21.26.10.0"),sQuery(id+"F5.wireOp",EDGE,"E21.29.10.0"),sQuery(id+"F5.wireOp",EDGE,"E21.32.10.0"),sQuery(id+"F5.wireOp",EDGE,"E21.36.10.0"),sQuery(id+"F5.wireOp",EDGE,"E21.37.10.0"),sQuery(id+"F5.wireOp",EDGE,"E21.39.10.0"),sQuery(id+"F5.wireOp",EDGE,"E21.42.10.0"),sQuery(id+"F5.wireOp",EDGE,"E21.46.10.0"),sQuery(id+"F5.wireOp",EDGE,"E21.49.10.0"),sQuery(id+"F5.wireOp",EDGE,"E21.52.10.0"),sQuery(id+"F5.wireOp",EDGE,"E21.4.11.0"),sQuery(id+"F5.wireOp",EDGE,"E21.8.11.0"),sQuery(id+"F5.wireOp",EDGE,"E21.12.11.0"),sQuery(id+"F5.wireOp",EDGE,"E21.16.11.0"),sQuery(id+"F5.wireOp",EDGE,"E21.19.11.0"),sQuery(id+"F5.wireOp",EDGE,"E21.22.11.0"),sQuery(id+"F5.wireOp",EDGE,"E21.26.11.0"),sQuery(id+"F5.wireOp",EDGE,"E21.29.11.0"),sQuery(id+"F5.wireOp",EDGE,"E21.32.11.0"),sQuery(id+"F5.wireOp",EDGE,"E21.36.11.0"),sQuery(id+"F5.wireOp",EDGE,"E21.37.11.0"),sQuery(id+"F5.wireOp",EDGE,"E21.39.11.0"),sQuery(id+"F5.wireOp",EDGE,"E21.42.11.0"),sQuery(id+"F5.wireOp",EDGE,"E21.46.11.0"),sQuery(id+"F5.wireOp",EDGE,"E21.49.11.0"),sQuery(id+"F5.wireOp",EDGE,"E21.52.11.0")])],"isStart":true});
            chamfer(context, id + "F7", {"entities" : qUnion([Q0]), "width" : 1 * mm, "tangentPropagation" : true});
        }
        {
            var Q0;
            Q0=makeQuery(id+"F6.opExtrude","CAP_FACE",FACE,{"disambiguationData":[OSD([sQuery(id+"F5.wireOp",EDGE,"E3"),sQuery(id+"F5.wireOp",EDGE,"E4"),sQuery(id+"F5.wireOp",EDGE,"E5"),sQuery(id+"F5.wireOp",EDGE,"E6.MirrorCS"),sQuery(id+"F5.wireOp",EDGE,"E7"),sQuery(id+"F5.wireOp",EDGE,"E8"),sQuery(id+"F5.wireOp",EDGE,"E9"),sQuery(id+"F5.wireOp",EDGE,"E10"),sQuery(id+"F5.wireOp",EDGE,"E11"),sQuery(id+"F5.wireOp",EDGE,"E12"),sQuery(id+"F5.wireOp",EDGE,"E13"),sQuery(id+"F5.wireOp",EDGE,"E14.trimOffspring"),sQuery(id+"F5.wireOp",EDGE,"E15.trimOffspring"),sQuery(id+"F5.wireOp",EDGE,"E16.trimOffspring"),sQuery(id+"F5.wireOp",EDGE,"E17.trimOffspring"),sQuery(id+"F5.wireOp",EDGE,"E18.trimOffspring"),sQuery(id+"F5.wireOp",EDGE,"E19.trimOffspring"),sQuery(id+"F5.wireOp",EDGE,"E20.1.0"),sQuery(id+"F5.wireOp",EDGE,"E20.1.1"),sQuery(id+"F5.wireOp",EDGE,"E20.1.2"),sQuery(id+"F5.wireOp",EDGE,"E20.1.3"),sQuery(id+"F5.wireOp",EDGE,"E20.1.4"),sQuery(id+"F5.wireOp",EDGE,"E20.1.5"),sQuery(id+"F5.wireOp",EDGE,"E20.1.6"),sQuery(id+"F5.wireOp",EDGE,"E20.1.7"),sQuery(id+"F5.wireOp",EDGE,"E20.1.8"),sQuery(id+"F5.wireOp",EDGE,"E20.1.9"),sQuery(id+"F5.wireOp",EDGE,"E20.1.10"),sQuery(id+"F5.wireOp",EDGE,"E20.1.11"),sQuery(id+"F5.wireOp",EDGE,"E20.1.12"),sQuery(id+"F5.wireOp",EDGE,"E20.1.13"),sQuery(id+"F5.wireOp",EDGE,"E20.1.14"),sQuery(id+"F5.wireOp",EDGE,"E20.1.15"),sQuery(id+"F5.wireOp",EDGE,"E20.2.0"),sQuery(id+"F5.wireOp",EDGE,"E20.2.1"),sQuery(id+"F5.wireOp",EDGE,"E20.2.2"),sQuery(id+"F5.wireOp",EDGE,"E20.2.3"),sQuery(id+"F5.wireOp",EDGE,"E20.2.4"),sQuery(id+"F5.wireOp",EDGE,"E20.2.5"),sQuery(id+"F5.wireOp",EDGE,"E20.2.6"),sQuery(id+"F5.wireOp",EDGE,"E20.2.7"),sQuery(id+"F5.wireOp",EDGE,"E20.2.8"),sQuery(id+"F5.wireOp",EDGE,"E20.2.9"),sQuery(id+"F5.wireOp",EDGE,"E20.2.10"),sQuery(id+"F5.wireOp",EDGE,"E20.2.11"),sQuery(id+"F5.wireOp",EDGE,"E20.2.12"),sQuery(id+"F5.wireOp",EDGE,"E20.2.13"),sQuery(id+"F5.wireOp",EDGE,"E20.2.14"),sQuery(id+"F5.wireOp",EDGE,"E20.2.15"),sQuery(id+"F5.wireOp",EDGE,"E20.3.0"),sQuery(id+"F5.wireOp",EDGE,"E20.3.1"),sQuery(id+"F5.wireOp",EDGE,"E20.3.2"),sQuery(id+"F5.wireOp",EDGE,"E20.3.3"),sQuery(id+"F5.wireOp",EDGE,"E20.3.4"),sQuery(id+"F5.wireOp",EDGE,"E20.3.5"),sQuery(id+"F5.wireOp",EDGE,"E20.3.6"),sQuery(id+"F5.wireOp",EDGE,"E20.3.7"),sQuery(id+"F5.wireOp",EDGE,"E20.3.8"),sQuery(id+"F5.wireOp",EDGE,"E20.3.9"),sQuery(id+"F5.wireOp",EDGE,"E20.3.10"),sQuery(id+"F5.wireOp",EDGE,"E20.3.11"),sQuery(id+"F5.wireOp",EDGE,"E20.3.12"),sQuery(id+"F5.wireOp",EDGE,"E20.3.13"),sQuery(id+"F5.wireOp",EDGE,"E20.3.14"),sQuery(id+"F5.wireOp",EDGE,"E20.3.15"),sQuery(id+"F5.wireOp",EDGE,"E20.4.0"),sQuery(id+"F5.wireOp",EDGE,"E20.4.1"),sQuery(id+"F5.wireOp",EDGE,"E20.4.2"),sQuery(id+"F5.wireOp",EDGE,"E20.4.3"),sQuery(id+"F5.wireOp",EDGE,"E20.4.4"),sQuery(id+"F5.wireOp",EDGE,"E20.4.5"),sQuery(id+"F5.wireOp",EDGE,"E20.4.6"),sQuery(id+"F5.wireOp",EDGE,"E20.4.7"),sQuery(id+"F5.wireOp",EDGE,"E20.4.8"),sQuery(id+"F5.wireOp",EDGE,"E20.4.9"),sQuery(id+"F5.wireOp",EDGE,"E20.4.10"),sQuery(id+"F5.wireOp",EDGE,"E20.4.11"),sQuery(id+"F5.wireOp",EDGE,"E20.4.12"),sQuery(id+"F5.wireOp",EDGE,"E20.4.13"),sQuery(id+"F5.wireOp",EDGE,"E20.4.14"),sQuery(id+"F5.wireOp",EDGE,"E20.4.15"),sQuery(id+"F5.wireOp",EDGE,"E20.5.0"),sQuery(id+"F5.wireOp",EDGE,"E20.5.1"),sQuery(id+"F5.wireOp",EDGE,"E20.5.2"),sQuery(id+"F5.wireOp",EDGE,"E20.5.3"),sQuery(id+"F5.wireOp",EDGE,"E20.5.4"),sQuery(id+"F5.wireOp",EDGE,"E20.5.5"),sQuery(id+"F5.wireOp",EDGE,"E20.5.6"),sQuery(id+"F5.wireOp",EDGE,"E20.5.7"),sQuery(id+"F5.wireOp",EDGE,"E20.5.8"),sQuery(id+"F5.wireOp",EDGE,"E20.5.9"),sQuery(id+"F5.wireOp",EDGE,"E20.5.10"),sQuery(id+"F5.wireOp",EDGE,"E20.5.11"),sQuery(id+"F5.wireOp",EDGE,"E20.5.12"),sQuery(id+"F5.wireOp",EDGE,"E20.5.13"),sQuery(id+"F5.wireOp",EDGE,"E20.5.14"),sQuery(id+"F5.wireOp",EDGE,"E20.5.15"),sQuery(id+"F5.wireOp",EDGE,"E20.6.0"),sQuery(id+"F5.wireOp",EDGE,"E20.6.1"),sQuery(id+"F5.wireOp",EDGE,"E20.6.2"),sQuery(id+"F5.wireOp",EDGE,"E20.6.3"),sQuery(id+"F5.wireOp",EDGE,"E20.6.4"),sQuery(id+"F5.wireOp",EDGE,"E20.6.5"),sQuery(id+"F5.wireOp",EDGE,"E20.6.6"),sQuery(id+"F5.wireOp",EDGE,"E20.6.7"),sQuery(id+"F5.wireOp",EDGE,"E20.6.8"),sQuery(id+"F5.wireOp",EDGE,"E20.6.9"),sQuery(id+"F5.wireOp",EDGE,"E20.6.10"),sQuery(id+"F5.wireOp",EDGE,"E20.6.11"),sQuery(id+"F5.wireOp",EDGE,"E20.6.12"),sQuery(id+"F5.wireOp",EDGE,"E20.6.13"),sQuery(id+"F5.wireOp",EDGE,"E20.6.14"),sQuery(id+"F5.wireOp",EDGE,"E20.6.15"),sQuery(id+"F5.wireOp",EDGE,"E20.7.0"),sQuery(id+"F5.wireOp",EDGE,"E20.7.1"),sQuery(id+"F5.wireOp",EDGE,"E20.7.2"),sQuery(id+"F5.wireOp",EDGE,"E20.7.3"),sQuery(id+"F5.wireOp",EDGE,"E20.7.4"),sQuery(id+"F5.wireOp",EDGE,"E20.7.5"),sQuery(id+"F5.wireOp",EDGE,"E20.7.6"),sQuery(id+"F5.wireOp",EDGE,"E20.7.7"),sQuery(id+"F5.wireOp",EDGE,"E20.7.8"),sQuery(id+"F5.wireOp",EDGE,"E20.7.9"),sQuery(id+"F5.wireOp",EDGE,"E20.7.10"),sQuery(id+"F5.wireOp",EDGE,"E20.7.11"),sQuery(id+"F5.wireOp",EDGE,"E20.7.12"),sQuery(id+"F5.wireOp",EDGE,"E20.7.13"),sQuery(id+"F5.wireOp",EDGE,"E20.7.14"),sQuery(id+"F5.wireOp",EDGE,"E20.7.15"),sQuery(id+"F5.wireOp",EDGE,"E20.8.0"),sQuery(id+"F5.wireOp",EDGE,"E20.8.1"),sQuery(id+"F5.wireOp",EDGE,"E20.8.2"),sQuery(id+"F5.wireOp",EDGE,"E20.8.3"),sQuery(id+"F5.wireOp",EDGE,"E20.8.4"),sQuery(id+"F5.wireOp",EDGE,"E20.8.5"),sQuery(id+"F5.wireOp",EDGE,"E20.8.6"),sQuery(id+"F5.wireOp",EDGE,"E20.8.7"),sQuery(id+"F5.wireOp",EDGE,"E20.8.8"),sQuery(id+"F5.wireOp",EDGE,"E20.8.9"),sQuery(id+"F5.wireOp",EDGE,"E20.8.10"),sQuery(id+"F5.wireOp",EDGE,"E20.8.11"),sQuery(id+"F5.wireOp",EDGE,"E20.8.12"),sQuery(id+"F5.wireOp",EDGE,"E20.8.13"),sQuery(id+"F5.wireOp",EDGE,"E20.8.14"),sQuery(id+"F5.wireOp",EDGE,"E20.8.15"),sQuery(id+"F5.wireOp",EDGE,"E20.9.0"),sQuery(id+"F5.wireOp",EDGE,"E20.9.1"),sQuery(id+"F5.wireOp",EDGE,"E20.9.2"),sQuery(id+"F5.wireOp",EDGE,"E20.9.3"),sQuery(id+"F5.wireOp",EDGE,"E20.9.4"),sQuery(id+"F5.wireOp",EDGE,"E20.9.5"),sQuery(id+"F5.wireOp",EDGE,"E20.9.6"),sQuery(id+"F5.wireOp",EDGE,"E20.9.7"),sQuery(id+"F5.wireOp",EDGE,"E20.9.8"),sQuery(id+"F5.wireOp",EDGE,"E20.9.9"),sQuery(id+"F5.wireOp",EDGE,"E20.9.10"),sQuery(id+"F5.wireOp",EDGE,"E20.9.11"),sQuery(id+"F5.wireOp",EDGE,"E20.9.12"),sQuery(id+"F5.wireOp",EDGE,"E20.9.13"),sQuery(id+"F5.wireOp",EDGE,"E20.9.14"),sQuery(id+"F5.wireOp",EDGE,"E20.9.15"),sQuery(id+"F5.wireOp",EDGE,"E21.4.10.0"),sQuery(id+"F5.wireOp",EDGE,"E21.8.10.0"),sQuery(id+"F5.wireOp",EDGE,"E21.12.10.0"),sQuery(id+"F5.wireOp",EDGE,"E21.16.10.0"),sQuery(id+"F5.wireOp",EDGE,"E21.19.10.0"),sQuery(id+"F5.wireOp",EDGE,"E21.22.10.0"),sQuery(id+"F5.wireOp",EDGE,"E21.26.10.0"),sQuery(id+"F5.wireOp",EDGE,"E21.29.10.0"),sQuery(id+"F5.wireOp",EDGE,"E21.32.10.0"),sQuery(id+"F5.wireOp",EDGE,"E21.36.10.0"),sQuery(id+"F5.wireOp",EDGE,"E21.37.10.0"),sQuery(id+"F5.wireOp",EDGE,"E21.39.10.0"),sQuery(id+"F5.wireOp",EDGE,"E21.42.10.0"),sQuery(id+"F5.wireOp",EDGE,"E21.46.10.0"),sQuery(id+"F5.wireOp",EDGE,"E21.49.10.0"),sQuery(id+"F5.wireOp",EDGE,"E21.52.10.0"),sQuery(id+"F5.wireOp",EDGE,"E21.4.11.0"),sQuery(id+"F5.wireOp",EDGE,"E21.8.11.0"),sQuery(id+"F5.wireOp",EDGE,"E21.12.11.0"),sQuery(id+"F5.wireOp",EDGE,"E21.16.11.0"),sQuery(id+"F5.wireOp",EDGE,"E21.19.11.0"),sQuery(id+"F5.wireOp",EDGE,"E21.22.11.0"),sQuery(id+"F5.wireOp",EDGE,"E21.26.11.0"),sQuery(id+"F5.wireOp",EDGE,"E21.29.11.0"),sQuery(id+"F5.wireOp",EDGE,"E21.32.11.0"),sQuery(id+"F5.wireOp",EDGE,"E21.36.11.0"),sQuery(id+"F5.wireOp",EDGE,"E21.37.11.0"),sQuery(id+"F5.wireOp",EDGE,"E21.39.11.0"),sQuery(id+"F5.wireOp",EDGE,"E21.42.11.0"),sQuery(id+"F5.wireOp",EDGE,"E21.46.11.0"),sQuery(id+"F5.wireOp",EDGE,"E21.49.11.0"),sQuery(id+"F5.wireOp",EDGE,"E21.52.11.0")])],"isStart":false});
            var sketch = newSketch(context, id + "F8", { "sketchPlane" : qUnion([Q0])});
            skCircle(sketch, "E22", {"center": v(16.16, 60.3) * mm, "radius": 5 * mm});
            skLineSegment(sketch, "E23", {"start": v(16.16, 60.3) * mm, "end": v(0, 0) * mm});
            skCircle(sketch, "E24.1.0", {"center": v(-44.15, 44.15) * mm, "radius": 5 * mm});
            skCircle(sketch, "E24.2.0", {"center": v(-60.3, -16.16) * mm, "radius": 5 * mm});
            skCircle(sketch, "E24.3.0", {"center": v(-16.16, -60.3) * mm, "radius": 5 * mm});
            skCircle(sketch, "E24.4.0", {"center": v(44.15, -44.15) * mm, "radius": 5 * mm});
            skCircle(sketch, "E24.5.0", {"center": v(60.3, 16.16) * mm, "radius": 5 * mm});
            skPoint(sketch, "E24.center", {"position": v(0, 0) * mm});
            skSolve(sketch);
        }
        {
            var Q0;
            Q0 = qSketchRegion(id + "F8", true);
            extrude(context, id + "F9", {"entities" : qUnion([Q0]), "operationType" : NewBodyOperationType.ADD, "depth" : 25 * mm, "offsetDistance" : 25 * mm});
        }
        {
            var Q0;
            Q0=makeQuery(id+"F9.opExtrude","CAP_FACE",FACE,{"disambiguationData":[OSD([sQuery(id+"F8.wireOp",EDGE,"E24.1.0")])],"isStart":false});
            var Q1;
            Q1=makeQuery(id+"F9.opExtrude","CAP_FACE",FACE,{"disambiguationData":[OSD([sQuery(id+"F8.wireOp",EDGE,"E22")])],"isStart":false});
            var Q2;
            Q2=makeQuery(id+"F9.opExtrude","CAP_FACE",FACE,{"disambiguationData":[OSD([sQuery(id+"F8.wireOp",EDGE,"E24.5.0")])],"isStart":false});
            var Q3;
            Q3=makeQuery(id+"F9.opExtrude","CAP_FACE",FACE,{"disambiguationData":[OSD([sQuery(id+"F8.wireOp",EDGE,"E24.4.0")])],"isStart":false});
            var Q4;
            Q4=makeQuery(id+"F9.opExtrude","CAP_FACE",FACE,{"disambiguationData":[OSD([sQuery(id+"F8.wireOp",EDGE,"E24.3.0")])],"isStart":false});
            var Q5;
            Q5=makeQuery(id+"F9.opExtrude","CAP_FACE",FACE,{"disambiguationData":[OSD([sQuery(id+"F8.wireOp",EDGE,"E24.2.0")])],"isStart":false});
            chamfer(context, id + "F10", {"entities" : qUnion([Q0, Q1, Q2, Q3, Q4, Q5]), "width" : 3 * mm, "tangentPropagation" : true});
        }
    });
